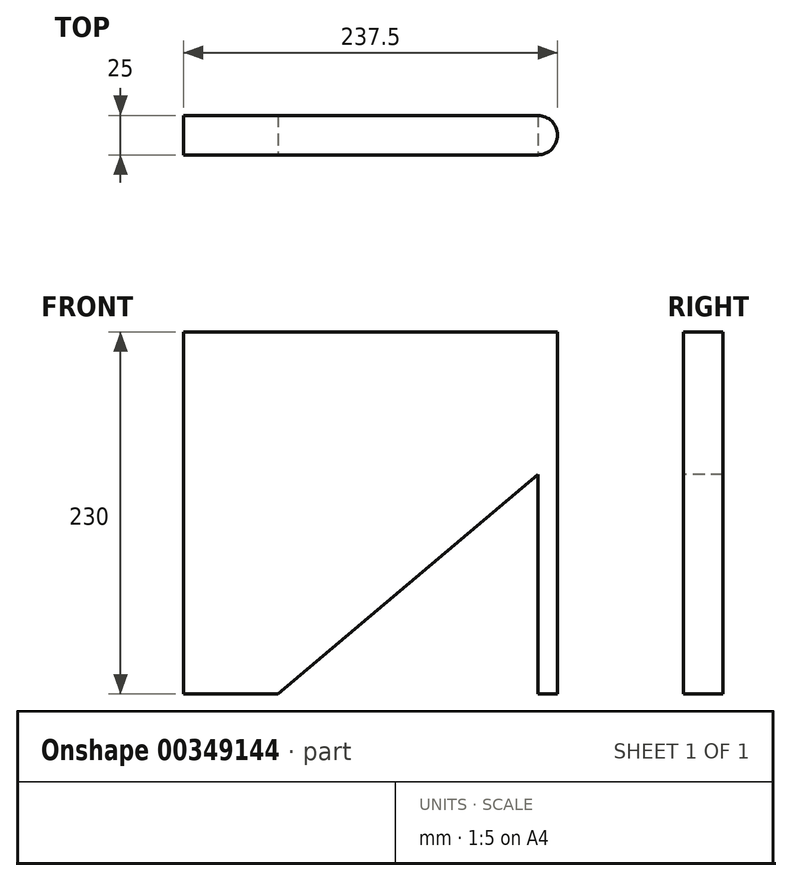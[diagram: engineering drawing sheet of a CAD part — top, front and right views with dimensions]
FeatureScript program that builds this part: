
annotation { "Feature Type Name" : "Feature", "Feature Type Description" : "" }
export const myFeature = defineFeature(function(context is Context, id is Id, definition is map)
    precondition{}
    {
        {
            var Q0;
            Q0=qCreatedBy(makeId("Top.planeOp"),FACE);
            var sketch = newSketch(context, id + "F0", { "sketchPlane" : qUnion([Q0])});
            skLineSegment(sketch, "E0.bottom", {"start": v(0, 0) * mm, "end": v(225, 0) * mm});
            skLineSegment(sketch, "E0.top", {"start": v(0, 25) * mm, "end": v(225, 25) * mm});
            skLineSegment(sketch, "E0.left", {"start": v(0, 0) * mm, "end": v(0, 25) * mm});
            skArc(sketch, "E1", {"start": v(225, 0) * mm, "mid": v(237.5, 12.5) * mm, "end": v(225, 25) * mm});
            skSolve(sketch);
        }
        {
            var Q0;
            Q0=makeQuery(id+"F0.imprint","IMPRINT",FACE,{"disambiguationData":[TD([[makeQuery(id+"F0.imprint","IMPRINT",EDGE,{"derivedFrom":sQuery(id+"F0.wireOp",EDGE,"E0.bottom")}),1.0]])]});
            extrude(context, id + "F1", {"entities" : qUnion([Q0]), "depth" : 230 * mm});
        }
        {
            var Q0;
            Q0=makeQuery(id+"F1.opExtrude","SWEPT_FACE",FACE,{"disambiguationData":[OSD([sQuery(id+"F0.wireOp",EDGE,"E0.bottom")])]});
            var sketch = newSketch(context, id + "F2", { "sketchPlane" : qUnion([Q0])});
            skLineSegment(sketch, "E2", {"start": v(237.5, 191.8) * mm, "end": v(237.5, 0) * mm});
            skLineSegment(sketch, "E3", {"start": v(237.5, 150) * mm, "end": v(60, 0) * mm});
            skLineSegment(sketch, "E4", {"start": v(60, 0) * mm, "end": v(237.5, 0) * mm});
            skLineSegment(sketch, "E5", {"start": v(237.5, 150) * mm, "end": v(237.5, 0) * mm});
            skSolve(sketch);
        }
        {
            var Q0;
            {var subQ0=sQuery(id+"F2.wireOp",EDGE,"E5");Q0=makeQuery(id+"F2.imprint","IMPRINT",FACE,{"disambiguationData":[TD([[makeQuery(id+"F2.imprint","IMPRINT",EDGE,{"derivedFrom":subQ0}),-1.0]])]});}
            var Q1;
            {var subQ0=sQuery(id+"F2.wireOp",EDGE,"E4");var subQ1=sQuery(id+"F2.wireOp",EDGE,"E3");var subQ2=sQuery(id+"F0.wireOp",EDGE,"E0.bottom");var subQ3=makeQuery(id+"F2.imprint","INTERSECT",VERTEX,{"derivedFrom":[makeQuery(id+"F1.opExtrude","CAP_EDGE",EDGE,{"disambiguationData":[OSD([subQ2])],"isStart":true}),subQ1,subQ0]});Q1=makeQuery(id+"F2.imprint","IMPRINT",FACE,{"disambiguationData":[TD([[makeQuery(id+"F2.imprint","IMPRINT",EDGE,{"disambiguationData":[TD([[subQ3,1.0]])],"derivedFrom":subQ1}),1.0]])]});}
            extrude(context, id + "F3", {"entities" : qUnion([Q0, Q1]), "operationType" : NewBodyOperationType.REMOVE, "endBound" : BoundingType.THROUGH_ALL, "oppositeDirection" : true, "depth" : 25 * mm});
        }
    });
